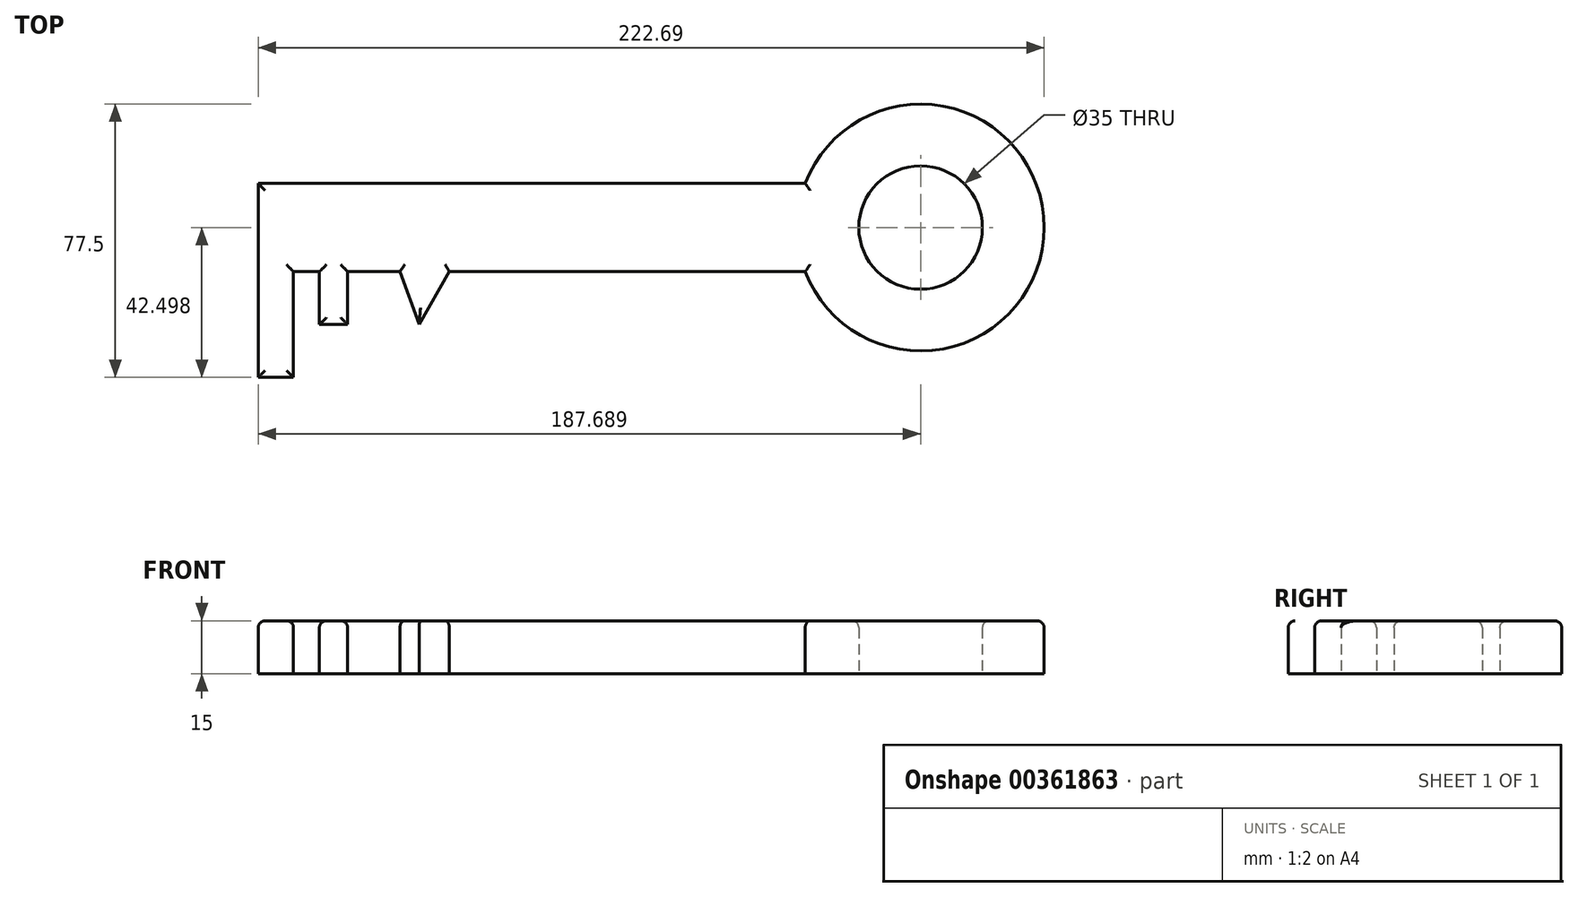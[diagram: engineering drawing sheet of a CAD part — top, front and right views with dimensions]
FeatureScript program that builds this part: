
annotation { "Feature Type Name" : "Feature", "Feature Type Description" : "" }
export const myFeature = defineFeature(function(context is Context, id is Id, definition is map)
    precondition{}
    {
        {
            var Q0;
            Q0=qCreatedBy(makeId("Top.planeOp"),FACE);
            var sketch = newSketch(context, id + "F0", { "sketchPlane" : qUnion([Q0])});
            skLineSegment(sketch, "E0.bottom", {"start": v(-111.43, 1.63) * mm, "end": v(43.57, 1.63) * mm});
            skLineSegment(sketch, "E0.top", {"start": v(-111.43, -23.37) * mm, "end": v(43.57, -23.37) * mm});
            skLineSegment(sketch, "E0.left", {"start": v(-111.43, 1.63) * mm, "end": v(-111.43, -23.37) * mm});
            skLineSegment(sketch, "E0.right", {"start": v(43.57, 1.63) * mm, "end": v(43.57, -23.37) * mm});
            skLineSegment(sketch, "E1.bottom", {"start": v(-111.43, -23.37) * mm, "end": v(-101.43, -23.37) * mm});
            skLineSegment(sketch, "E1.top", {"start": v(-111.43, -53.37) * mm, "end": v(-101.43, -53.37) * mm});
            skLineSegment(sketch, "E1.left", {"start": v(-111.43, -23.37) * mm, "end": v(-111.43, -53.37) * mm});
            skLineSegment(sketch, "E1.right", {"start": v(-101.43, -23.37) * mm, "end": v(-101.43, -53.37) * mm});
            skLineSegment(sketch, "E2.bottom", {"start": v(-94.08, -23.37) * mm, "end": v(-86.08, -23.37) * mm});
            skLineSegment(sketch, "E2.top", {"start": v(-94.08, -38.37) * mm, "end": v(-86.08, -38.37) * mm});
            skLineSegment(sketch, "E2.left", {"start": v(-94.08, -23.37) * mm, "end": v(-94.08, -38.37) * mm});
            skLineSegment(sketch, "E2.right", {"start": v(-86.08, -23.37) * mm, "end": v(-86.08, -38.37) * mm});
            skLineSegment(sketch, "E3", {"start": v(-71.28, -23.37) * mm, "end": v(-65.84, -38.37) * mm});
            skLineSegment(sketch, "E4", {"start": v(-65.84, -38.37) * mm, "end": v(-57.28, -23.37) * mm});
            skLineSegment(sketch, "E5", {"start": v(-71.28, -23.37) * mm, "end": v(-57.28, -23.37) * mm});
            skArc(sketch, "E6", {"start": v(43.57, -23.37) * mm, "mid": v(111.26, -10.87) * mm, "end": v(43.57, 1.63) * mm});
            skCircle(sketch, "E7", {"center": v(76.26, -10.87) * mm, "radius": 17.5 * mm});
            skLineSegment(sketch, "E8", {"start": v(-111.43, -10.87) * mm, "end": v(76.26, -10.87) * mm, "construction": true});
            skSolve(sketch);
        }
        {
            var Q0;
            Q0 = qSketchRegion(id + "F0", true);
            extrude(context, id + "F1", {"entities" : qUnion([Q0]), "depth" : 15 * mm});
        }
        {
            var Q0;
            Q0=makeQuery(id+"F1.opExtrude","CAP_FACE",FACE,{"disambiguationData":[OSD([sQuery(id+"F0.wireOp",EDGE,"E0.bottom"),sQuery(id+"F0.wireOp",EDGE,"E0.top"),sQuery(id+"F0.wireOp",EDGE,"E0.left"),sQuery(id+"F0.wireOp",EDGE,"E1.top"),sQuery(id+"F0.wireOp",EDGE,"E1.left"),sQuery(id+"F0.wireOp",EDGE,"E1.right"),sQuery(id+"F0.wireOp",EDGE,"E2.top"),sQuery(id+"F0.wireOp",EDGE,"E2.left"),sQuery(id+"F0.wireOp",EDGE,"E2.right"),sQuery(id+"F0.wireOp",EDGE,"E3"),sQuery(id+"F0.wireOp",EDGE,"E4"),sQuery(id+"F0.wireOp",EDGE,"E6"),sQuery(id+"F0.wireOp",EDGE,"E7")])],"isStart":false});
            var Q1;
            Q1=makeQuery(id+"F1.opExtrude","CAP_EDGE",EDGE,{"disambiguationData":[OSD([sQuery(id+"F0.wireOp",EDGE,"E1.right")])],"isStart":false});
            var Q2;
            {var subQ0=sQuery(id+"F0.wireOp",EDGE,"E0.top");Q2=makeQuery(id+"F1.opExtrude","CAP_EDGE",EDGE,{"disambiguationData":[OSD([subQ0]),TDD([makeQuery(id+"F0.imprint","IMPRINT",EDGE,{"disambiguationData":[TD([[makeQuery(id+"F0.imprint","INTERSECT",VERTEX,{"derivedFrom":[subQ0,sQuery(id+"F0.wireOp",EDGE,"E1.bottom"),sQuery(id+"F0.wireOp",EDGE,"E1.right")]}),-1.0]])],"derivedFrom":subQ0})])],"isStart":false});}
            var Q3;
            Q3=makeQuery(id+"F1.opExtrude","CAP_EDGE",EDGE,{"disambiguationData":[OSD([sQuery(id+"F0.wireOp",EDGE,"E2.left")])],"isStart":false});
            var Q4;
            Q4=makeQuery(id+"F1.opExtrude","CAP_EDGE",EDGE,{"disambiguationData":[OSD([sQuery(id+"F0.wireOp",EDGE,"E2.top")])],"isStart":false});
            var Q5;
            Q5=makeQuery(id+"F1.opExtrude","CAP_EDGE",EDGE,{"disambiguationData":[OSD([sQuery(id+"F0.wireOp",EDGE,"E2.right")])],"isStart":false});
            var Q6;
            {var subQ0=sQuery(id+"F0.wireOp",EDGE,"E0.top");Q6=makeQuery(id+"F1.opExtrude","CAP_EDGE",EDGE,{"disambiguationData":[OSD([subQ0]),TDD([makeQuery(id+"F0.imprint","IMPRINT",EDGE,{"disambiguationData":[TD([[makeQuery(id+"F0.imprint","INTERSECT",VERTEX,{"derivedFrom":[subQ0,sQuery(id+"F0.wireOp",EDGE,"E2.bottom"),sQuery(id+"F0.wireOp",EDGE,"E2.right")]}),-1.0]])],"derivedFrom":subQ0})])],"isStart":false});}
            var Q7;
            Q7=makeQuery(id+"F1.opExtrude","CAP_EDGE",EDGE,{"disambiguationData":[OSD([sQuery(id+"F0.wireOp",EDGE,"E3")])],"isStart":false});
            var Q8;
            {var subQ0=sQuery(id+"F0.wireOp",EDGE,"E0.top");Q8=makeQuery(id+"F1.opExtrude","CAP_EDGE",EDGE,{"disambiguationData":[OSD([subQ0]),TDD([makeQuery(id+"F0.imprint","IMPRINT",EDGE,{"disambiguationData":[TD([[makeQuery(id+"F0.imprint","INTERSECT",VERTEX,{"derivedFrom":[subQ0,sQuery(id+"F0.wireOp",EDGE,"E0.right"),sQuery(id+"F0.wireOp",EDGE,"E6")]}),1.0]])],"derivedFrom":subQ0})])],"isStart":false});}
            var Q9;
            Q9=makeQuery(id+"F1.opExtrude","CAP_EDGE",EDGE,{"disambiguationData":[OSD([sQuery(id+"F0.wireOp",EDGE,"E6")])],"isStart":false});
            var Q10;
            Q10=makeQuery(id+"F1.opExtrude","CAP_EDGE",EDGE,{"disambiguationData":[OSD([sQuery(id+"F0.wireOp",EDGE,"E7")])],"isStart":false});
            var Q11;
            Q11=makeQuery(id+"F1.opExtrude","CAP_EDGE",EDGE,{"disambiguationData":[OSD([sQuery(id+"F0.wireOp",EDGE,"E0.bottom")])],"isStart":false});
            var Q12;
            Q12=makeQuery(id+"F1.opExtrude","CAP_EDGE",EDGE,{"disambiguationData":[OSD([sQuery(id+"F0.wireOp",EDGE,"E0.left"),sQuery(id+"F0.wireOp",EDGE,"E1.left")])],"isStart":false});
            var Q13;
            Q13=makeQuery(id+"F1.opExtrude","CAP_EDGE",EDGE,{"disambiguationData":[OSD([sQuery(id+"F0.wireOp",EDGE,"E1.top")])],"isStart":false});
            fillet(context, id + "F2", {"entities" : qUnion([Q0, Q1, Q2, Q3, Q4, Q5, Q6, Q7, Q8, Q9, Q10, Q11, Q12, Q13]), "radius" : 2 * mm, "tangentPropagation" : true, "allowEdgeOverflow" : false});
        }
    });
